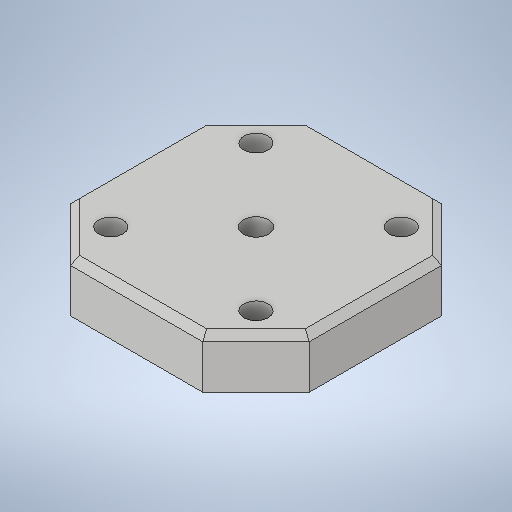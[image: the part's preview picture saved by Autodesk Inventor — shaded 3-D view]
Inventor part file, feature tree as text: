
AUTODESK INVENTOR PART (.ipt)
format: ipt  version: 2025 (Build 290162000, 162)  size: 293,376 bytes
history: native  units: in
note: dims shown in document units (in); Inventor stores cm internally (conversion verified against a paired STEP export)
features: extrude x3, chamfer x2, hole x1, sketch x1
ambient origin geometry x8: Origin, YZ Plane, XZ Plane, XY Plane, X Axis, Y Axis, Z Axis, Center Point
bodies: Solid1 (feature_tree)
feature tree (7):
  extrude  "Extrusion1"  Depth=1.122in
  hole  "Hole1"  [1 undecoded]
  extrude  "Extrusion2"  Depth=1.122in
  extrude  "Extrusion3"  Depth=0.25in TaperAngle=0.0deg
  chamfer  "Chamfer3"  Distance=0.059in
  chamfer  "Chamfer4"  Distance=0.0625in
  sketch  "Sketch Circular Pattern2"  dims[d0=1.122in d1=1.122in d2=0.2362in d3=0.0in d15=0.1142in d16=0.18in d17=0.375in d18=0.25in d19=0.5635in d20=0.22in d21=0.8108in d22=0.118in d23=0.25in d24=0.0in d27=0.059in d28=0.0in d42=0.0625in d45=0.25in d47=0.25in d48=0.125in d49=45.0deg d50=0.0312in d51=0.125in d52=45.0deg d57=0.125in d58=0.2165in d59=0.2165in d60=0.9646in d61=1.122in d62=0.561in d63=1.122in d64=0.561in d69=45.0deg d70=1.5748in d72=360.0deg]
note: 1 required parameter value undecoded (feature->parameter linkage not recoverable at this tier; creation-order binding heuristic only, values carry confidence <= 0.55)
